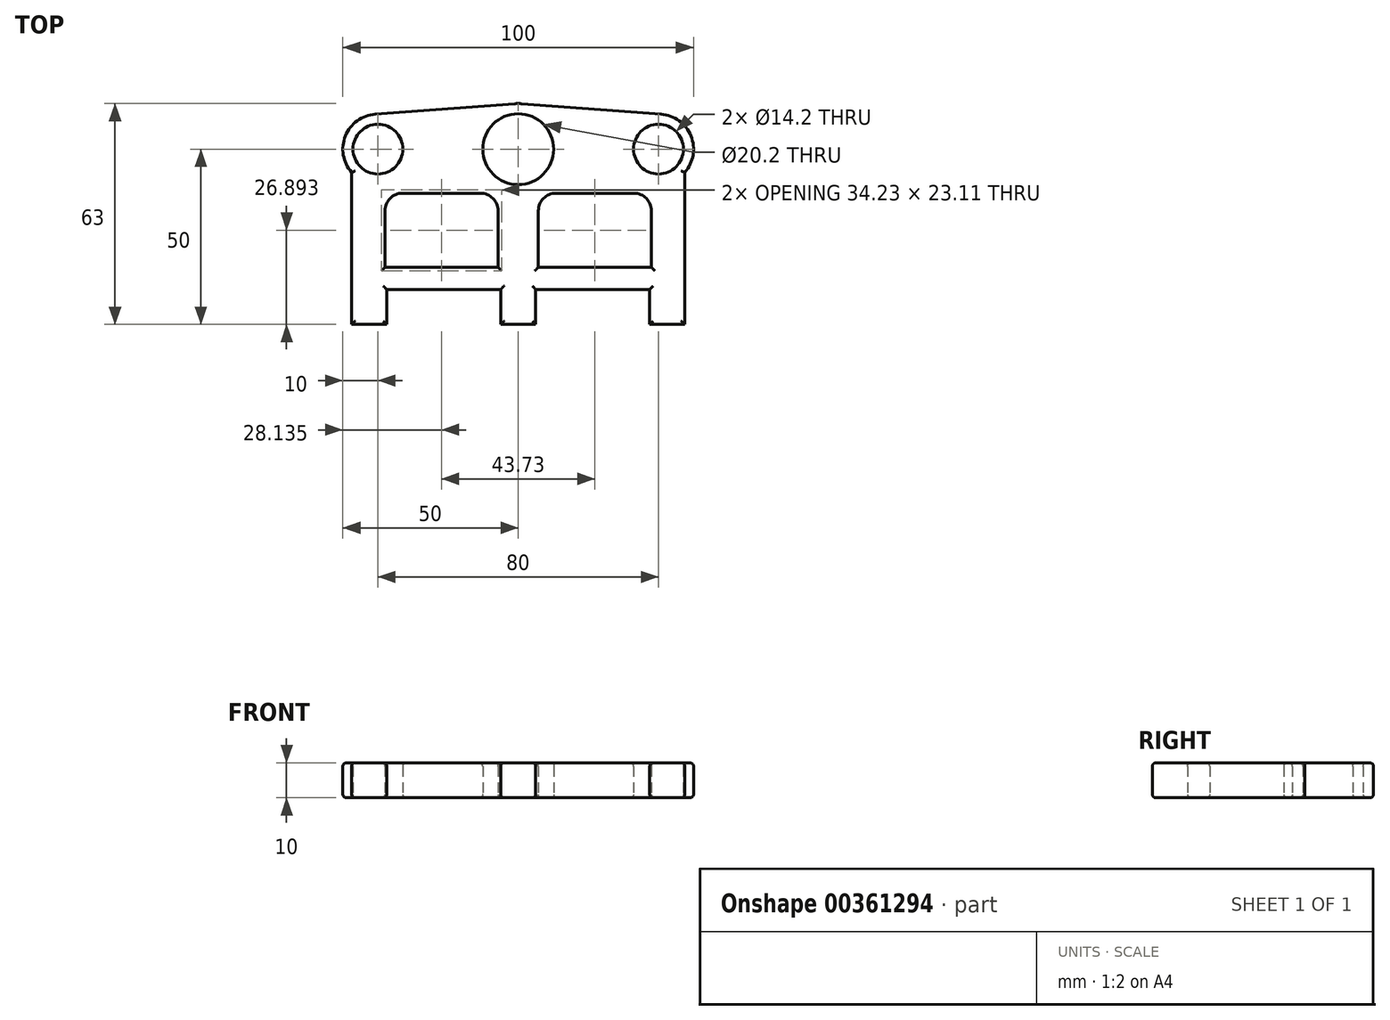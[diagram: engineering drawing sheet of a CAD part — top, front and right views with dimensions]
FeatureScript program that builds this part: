
annotation { "Feature Type Name" : "Feature", "Feature Type Description" : "" }
export const myFeature = defineFeature(function(context is Context, id is Id, definition is map)
    precondition{}
    {
        {
            var Q0;
            Q0=qCreatedBy(makeId("Top.planeOp"),FACE);
            var sketch = newSketch(context, id + "F0", { "sketchPlane" : qUnion([Q0])});
            skCircle(sketch, "E0", {"center": v(0, 0) * mm, "radius": 10.1 * mm});
            skLineSegment(sketch, "E1", {"start": v(0, 0) * mm, "end": v(-40, 0) * mm, "construction": true});
            skCircle(sketch, "E2", {"center": v(0, 0) * mm, "radius": 40 * mm, "construction": true});
            skLineSegment(sketch, "E3", {"start": v(-37.5, -40) * mm, "end": v(-5, -40) * mm});
            skArc(sketch, "E4", {"start": v(0.98, 12.96) * mm, "mid": v(0, 13) * mm, "end": v(-0.98, 12.96) * mm});
            skLineSegment(sketch, "E5.trimOffspring", {"start": v(-40, 7.5) * mm, "end": v(-40, 7.56) * mm});
            skPoint(sketch, "E6.visualSharp", {"position": v(-39.3, -7.47) * mm});
            skPoint(sketch, "E7.visualSharp", {"position": v(-9.91, -7.47) * mm});
            skLineSegment(sketch, "E8.top", {"start": v(-47.5, -50) * mm, "end": v(-37.5, -50) * mm});
            skLineSegment(sketch, "E8.left", {"start": v(-47.5, -40) * mm, "end": v(-47.5, -50) * mm});
            skLineSegment(sketch, "E8.right", {"start": v(-37.5, -40) * mm, "end": v(-37.5, -50) * mm});
            skLineSegment(sketch, "E9.top", {"start": v(47.5, -50) * mm, "end": v(37.5, -50) * mm});
            skLineSegment(sketch, "E9.left", {"start": v(47.5, -40) * mm, "end": v(47.5, -50) * mm});
            skLineSegment(sketch, "E9.right", {"start": v(37.5, -40) * mm, "end": v(37.5, -50) * mm});
            skLineSegment(sketch, "E10.top", {"start": v(0, -50) * mm, "end": v(-5, -50) * mm});
            skLineSegment(sketch, "E10.right", {"start": v(-5, -40) * mm, "end": v(-5, -50) * mm});
            skLineSegment(sketch, "E11.top", {"start": v(0, -50) * mm, "end": v(5, -50) * mm});
            skLineSegment(sketch, "E11.right", {"start": v(5, -40) * mm, "end": v(5, -50) * mm});
            skPoint(sketch, "E11.bottom.start.orphan", {"position": v(0, -40) * mm});
            skLineSegment(sketch, "E12.trimOffspring", {"start": v(5, -40) * mm, "end": v(37.5, -40) * mm});
            skCircle(sketch, "E13", {"center": v(40, 0) * mm, "radius": 7.1 * mm});
            skArc(sketch, "E14", {"start": v(47.5, -6.61) * mm, "mid": v(49.26, 3.77) * mm, "end": v(40.75, 9.97) * mm});
            skCircle(sketch, "E15", {"center": v(-40, 0) * mm, "radius": 7.1 * mm});
            skArc(sketch, "E16", {"start": v(-40.75, 9.97) * mm, "mid": v(-49.26, 3.77) * mm, "end": v(-47.5, -6.61) * mm});
            skLineSegment(sketch, "E17", {"start": v(47.5, -40) * mm, "end": v(47.5, -6.61) * mm});
            skLineSegment(sketch, "E18", {"start": v(-47.5, -40) * mm, "end": v(-47.5, -6.61) * mm});
            skLineSegment(sketch, "E19", {"start": v(-40.75, 9.97) * mm, "end": v(-0.97, 12.96) * mm});
            skLineSegment(sketch, "E20", {"start": v(0.97, 12.96) * mm, "end": v(40.75, 9.97) * mm});
            skLineSegment(sketch, "E21.bottom", {"start": v(-5.75, -33.66) * mm, "end": v(-37.98, -33.66) * mm});
            skLineSegment(sketch, "E21.top", {"start": v(-10.75, -12.55) * mm, "end": v(-32.98, -12.55) * mm});
            skLineSegment(sketch, "E21.left", {"start": v(-5.75, -33.66) * mm, "end": v(-5.75, -17.55) * mm});
            skLineSegment(sketch, "E21.right", {"start": v(-37.98, -33.66) * mm, "end": v(-37.98, -17.55) * mm});
            skPoint(sketch, "E22.visualSharp", {"position": v(-37.98, -33.66) * mm});
            skLineSegment(sketch, "E22.filletArc", {"start": v(-37.98, -33.66) * mm, "end": v(-37.98, -33.66) * mm});
            skPoint(sketch, "E23.visualSharp", {"position": v(-37.98, -12.55) * mm});
            skArc(sketch, "E23.filletArc", {"start": v(-32.98, -12.55) * mm, "mid": v(-36.51, -14.02) * mm, "end": v(-37.98, -17.55) * mm});
            skPoint(sketch, "E24.visualSharp", {"position": v(-5.75, -12.55) * mm});
            skArc(sketch, "E24.filletArc", {"start": v(-5.75, -17.55) * mm, "mid": v(-7.22, -14.02) * mm, "end": v(-10.75, -12.55) * mm});
            skLineSegment(sketch, "E25.MirrorCS", {"start": v(5.75, -33.66) * mm, "end": v(37.98, -33.66) * mm});
            skLineSegment(sketch, "E26.MirrorCS", {"start": v(37.98, -33.66) * mm, "end": v(37.98, -17.55) * mm});
            skLineSegment(sketch, "E27.MirrorCS", {"start": v(10.75, -12.55) * mm, "end": v(32.98, -12.55) * mm});
            skLineSegment(sketch, "E28.MirrorCS", {"start": v(5.75, -33.66) * mm, "end": v(5.75, -17.55) * mm});
            skArc(sketch, "E29.MirrorCS", {"start": v(5.75, -17.55) * mm, "mid": v(7.22, -14.02) * mm, "end": v(10.75, -12.55) * mm});
            skArc(sketch, "E30.MirrorCS", {"start": v(32.98, -12.55) * mm, "mid": v(36.51, -14.02) * mm, "end": v(37.98, -17.55) * mm});
            skSolve(sketch);
        }
        {
            var Q0;
            Q0=makeQuery(id+"F0.imprint","IMPRINT",FACE,{"disambiguationData":[TD([[makeQuery(id+"F0.imprint","IMPRINT",EDGE,{"derivedFrom":sQuery(id+"F0.wireOp",EDGE,"E0")}),-1.0]])]});
            var Q1;
            Q1=makeQuery(id+"F0.imprint","IMPRINT",FACE,{"disambiguationData":[TD([[makeQuery(id+"F0.imprint","IMPRINT",EDGE,{"derivedFrom":sQuery(id+"F0.wireOp",EDGE,"CpLtp0Nj-pjdu-8a4E-uumJ-denKsGrBu669")}),1.0]])]});
            extrude(context, id + "F1", {"entities" : qUnion([Q0, Q1]), "depth" : 10 * mm});
        }
        {
            var Q0;
            Q0=makeQuery(id+"F1.opExtrude","CAP_FACE",FACE,{"disambiguationData":[OSD([sQuery(id+"F0.wireOp",EDGE,"E0"),sQuery(id+"F0.wireOp",EDGE,"E3"),sQuery(id+"F0.wireOp",EDGE,"E4"),sQuery(id+"F0.wireOp",EDGE,"E8.top"),sQuery(id+"F0.wireOp",EDGE,"E8.left"),sQuery(id+"F0.wireOp",EDGE,"E8.right"),sQuery(id+"F0.wireOp",EDGE,"E9.top"),sQuery(id+"F0.wireOp",EDGE,"E9.left"),sQuery(id+"F0.wireOp",EDGE,"E9.right"),sQuery(id+"F0.wireOp",EDGE,"E10.top"),sQuery(id+"F0.wireOp",EDGE,"E10.right"),sQuery(id+"F0.wireOp",EDGE,"E11.top"),sQuery(id+"F0.wireOp",EDGE,"E11.right"),sQuery(id+"F0.wireOp",EDGE,"E12.trimOffspring"),sQuery(id+"F0.wireOp",EDGE,"E13"),sQuery(id+"F0.wireOp",EDGE,"E14"),sQuery(id+"F0.wireOp",EDGE,"E15"),sQuery(id+"F0.wireOp",EDGE,"E16"),sQuery(id+"F0.wireOp",EDGE,"E17"),sQuery(id+"F0.wireOp",EDGE,"E18"),sQuery(id+"F0.wireOp",EDGE,"E19"),sQuery(id+"F0.wireOp",EDGE,"E20"),sQuery(id+"F0.wireOp",EDGE,"E21.bottom"),sQuery(id+"F0.wireOp",EDGE,"E21.top"),sQuery(id+"F0.wireOp",EDGE,"E21.left"),sQuery(id+"F0.wireOp",EDGE,"E21.right"),sQuery(id+"F0.wireOp",EDGE,"E23.filletArc"),sQuery(id+"F0.wireOp",EDGE,"E24.filletArc"),sQuery(id+"F0.wireOp",EDGE,"E25.MirrorCS"),sQuery(id+"F0.wireOp",EDGE,"E26.MirrorCS"),sQuery(id+"F0.wireOp",EDGE,"E27.MirrorCS"),sQuery(id+"F0.wireOp",EDGE,"E28.MirrorCS"),sQuery(id+"F0.wireOp",EDGE,"E29.MirrorCS"),sQuery(id+"F0.wireOp",EDGE,"E30.MirrorCS")])],"isStart":false});
            var Q1;
            Q1=makeQuery(id+"F1.opExtrude","CAP_FACE",FACE,{"disambiguationData":[OSD([sQuery(id+"F0.wireOp",EDGE,"E0"),sQuery(id+"F0.wireOp",EDGE,"E3"),sQuery(id+"F0.wireOp",EDGE,"E4"),sQuery(id+"F0.wireOp",EDGE,"E8.top"),sQuery(id+"F0.wireOp",EDGE,"E8.left"),sQuery(id+"F0.wireOp",EDGE,"E8.right"),sQuery(id+"F0.wireOp",EDGE,"E9.top"),sQuery(id+"F0.wireOp",EDGE,"E9.left"),sQuery(id+"F0.wireOp",EDGE,"E9.right"),sQuery(id+"F0.wireOp",EDGE,"E10.top"),sQuery(id+"F0.wireOp",EDGE,"E10.right"),sQuery(id+"F0.wireOp",EDGE,"E11.top"),sQuery(id+"F0.wireOp",EDGE,"E11.right"),sQuery(id+"F0.wireOp",EDGE,"E12.trimOffspring"),sQuery(id+"F0.wireOp",EDGE,"E13"),sQuery(id+"F0.wireOp",EDGE,"E14"),sQuery(id+"F0.wireOp",EDGE,"E15"),sQuery(id+"F0.wireOp",EDGE,"E16"),sQuery(id+"F0.wireOp",EDGE,"E17"),sQuery(id+"F0.wireOp",EDGE,"E18"),sQuery(id+"F0.wireOp",EDGE,"E19"),sQuery(id+"F0.wireOp",EDGE,"E20"),sQuery(id+"F0.wireOp",EDGE,"E21.bottom"),sQuery(id+"F0.wireOp",EDGE,"E21.top"),sQuery(id+"F0.wireOp",EDGE,"E21.left"),sQuery(id+"F0.wireOp",EDGE,"E21.right"),sQuery(id+"F0.wireOp",EDGE,"E23.filletArc"),sQuery(id+"F0.wireOp",EDGE,"E24.filletArc"),sQuery(id+"F0.wireOp",EDGE,"E25.MirrorCS"),sQuery(id+"F0.wireOp",EDGE,"E26.MirrorCS"),sQuery(id+"F0.wireOp",EDGE,"E27.MirrorCS"),sQuery(id+"F0.wireOp",EDGE,"E28.MirrorCS"),sQuery(id+"F0.wireOp",EDGE,"E29.MirrorCS"),sQuery(id+"F0.wireOp",EDGE,"E30.MirrorCS")])],"isStart":true});
            fillet(context, id + "F2", {"entities" : qUnion([Q0, Q1]), "radius" : 1 * mm, "tangentPropagation" : true, "allowEdgeOverflow" : false});
        }
    });
